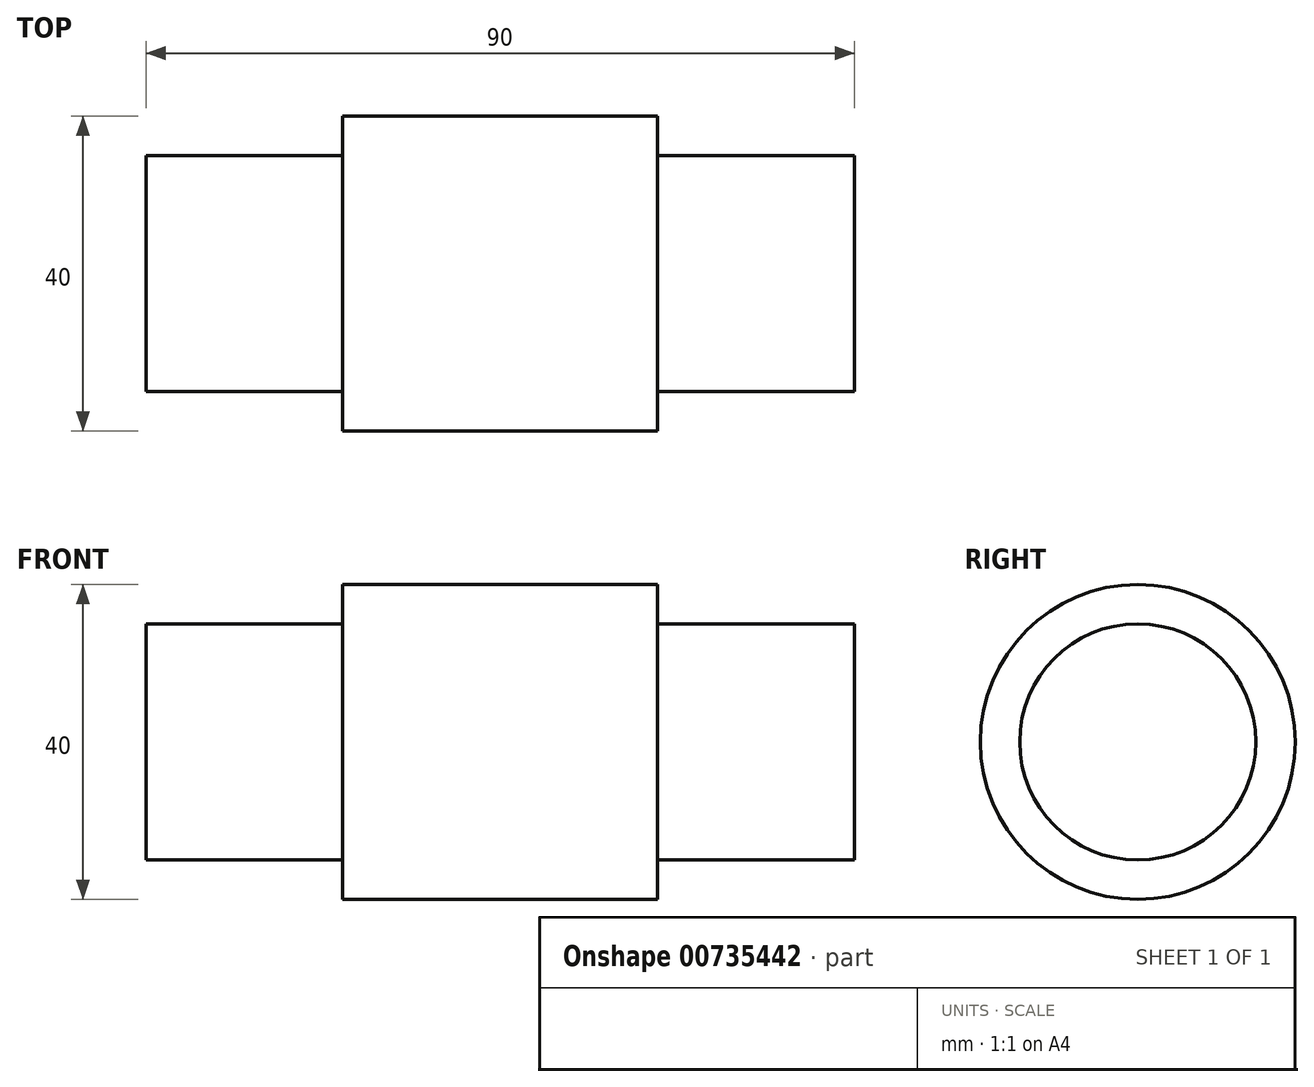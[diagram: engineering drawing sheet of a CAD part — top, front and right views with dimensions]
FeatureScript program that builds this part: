
annotation { "Feature Type Name" : "Feature", "Feature Type Description" : "" }
export const myFeature = defineFeature(function(context is Context, id is Id, definition is map)
    precondition{}
    {
        {
            var Q0;
            Q0=qCreatedBy(makeId("Top.planeOp"),FACE);
            var sketch = newSketch(context, id + "F0", { "sketchPlane" : qUnion([Q0])});
            skLineSegment(sketch, "E0", {"start": v(24.33, 1.06) * mm, "end": v(24.33, 16.06) * mm});
            skLineSegment(sketch, "E1", {"start": v(24.33, 16.06) * mm, "end": v(-25.67, 16.06) * mm});
            skLineSegment(sketch, "E2", {"start": v(24.33, 16.06) * mm, "end": v(19.33, 16.06) * mm});
            skLineSegment(sketch, "E3", {"start": v(-25.67, 16.06) * mm, "end": v(-20.67, 16.06) * mm});
            skLineSegment(sketch, "E4", {"start": v(-20.67, 16.06) * mm, "end": v(-15.67, 16.06) * mm});
            skLineSegment(sketch, "E5", {"start": v(19.33, 16.06) * mm, "end": v(14.33, 16.06) * mm});
            skPoint(sketch, "E6.1.internal.snap0", {"position": v(-0.67, 16.06) * mm});
            skLineSegment(sketch, "E7", {"start": v(19.33, 16.06) * mm, "end": v(19.33, 21.06) * mm});
            skLineSegment(sketch, "E8", {"start": v(24.33, 16.06) * mm, "end": v(19.33, 21.06) * mm});
            skLineSegment(sketch, "E9", {"start": v(19.33, 21.06) * mm, "end": v(-20.67, 21.06) * mm});
            skLineSegment(sketch, "E10", {"start": v(-20.67, 21.06) * mm, "end": v(-20.67, 16.06) * mm});
            skLineSegment(sketch, "E11", {"start": v(-20.67, 21.06) * mm, "end": v(-25.67, 16.06) * mm});
            skLineSegment(sketch, "E12", {"start": v(24.33, 1.06) * mm, "end": v(-25.67, 1.06) * mm});
            skLineSegment(sketch, "E13.MirrorCS", {"start": v(24.33, -13.94) * mm, "end": v(19.3, -13.94) * mm});
            skLineSegment(sketch, "E14.MirrorCS", {"start": v(24.3, -13.94) * mm, "end": v(19.3, -18.94) * mm});
            skLineSegment(sketch, "E15.MirrorCS", {"start": v(19.3, -13.94) * mm, "end": v(19.3, -18.94) * mm});
            skLineSegment(sketch, "E16.MirrorCS", {"start": v(-20.7, -18.94) * mm, "end": v(-25.7, -13.94) * mm});
            skLineSegment(sketch, "E17.MirrorCS", {"start": v(-20.7, -18.94) * mm, "end": v(-20.7, -13.94) * mm});
            skLineSegment(sketch, "E18.MirrorCS", {"start": v(-20.7, -13.94) * mm, "end": v(-15.7, -13.94) * mm});
            skLineSegment(sketch, "E19.MirrorCS", {"start": v(-25.7, -13.94) * mm, "end": v(-20.7, -13.94) * mm});
            skLineSegment(sketch, "E20.MirrorCS", {"start": v(19.3, -13.94) * mm, "end": v(14.3, -13.94) * mm});
            skLineSegment(sketch, "E21.MirrorCS", {"start": v(-25.67, 1.06) * mm, "end": v(-25.67, -13.94) * mm});
            skLineSegment(sketch, "E22.MirrorCS", {"start": v(24.3, -13.94) * mm, "end": v(-25.7, -13.94) * mm});
            skLineSegment(sketch, "E23.MirrorCS", {"start": v(19.3, -18.94) * mm, "end": v(-20.7, -18.94) * mm});
            skPoint(sketch, "E24.MirrorP", {"position": v(-0.67, -13.94) * mm});
            skLineSegment(sketch, "E25", {"start": v(24.33, 1.06) * mm, "end": v(24.33, -13.94) * mm});
            skLineSegment(sketch, "E26", {"start": v(-25.67, 16.06) * mm, "end": v(-25.67, 1.06) * mm});
            skLineSegment(sketch, "E27", {"start": v(-25.67, 16.06) * mm, "end": v(-45.67, 16.06) * mm});
            skLineSegment(sketch, "E28", {"start": v(-45.67, 16.06) * mm, "end": v(-45.67, -13.94) * mm});
            skLineSegment(sketch, "E29", {"start": v(-45.67, -13.94) * mm, "end": v(-25.7, -13.94) * mm});
            skLineSegment(sketch, "E30", {"start": v(-25.67, 1.06) * mm, "end": v(-45.67, 1.06) * mm});
            skLineSegment(sketch, "E31", {"start": v(24.33, 16.06) * mm, "end": v(44.33, 16.06) * mm});
            skLineSegment(sketch, "E32", {"start": v(24.33, -13.94) * mm, "end": v(44.33, -13.94) * mm});
            skLineSegment(sketch, "E33", {"start": v(44.33, -13.94) * mm, "end": v(44.33, 16.06) * mm});
            skLineSegment(sketch, "E34", {"start": v(24.33, 1.06) * mm, "end": v(44.33, 1.06) * mm});
            skSolve(sketch);
        }
        {
            var Q0;
            Q0=makeQuery(id+"F0.imprint","IMPRINT",FACE,{"disambiguationData":[TD([[makeQuery(id+"F0.imprint","IMPRINT",EDGE,{"derivedFrom":sQuery(id+"F0.wireOp",EDGE,"E3")}),1.0]])]});
            var Q1;
            Q1=makeQuery(id+"F0.imprint","IMPRINT",FACE,{"disambiguationData":[TD([[makeQuery(id+"F0.imprint","IMPRINT",EDGE,{"derivedFrom":sQuery(id+"F0.wireOp",EDGE,"E1")}),-1.0]])]});
            var Q2;
            Q2=makeQuery(id+"F0.imprint","IMPRINT",FACE,{"disambiguationData":[TD([[makeQuery(id+"F0.imprint","IMPRINT",EDGE,{"derivedFrom":sQuery(id+"F0.wireOp",EDGE,"E2")}),-1.0]])]});
            var Q3;
            Q3=makeQuery(id+"F0.imprint","IMPRINT",FACE,{"disambiguationData":[TD([[makeQuery(id+"F0.imprint","IMPRINT",EDGE,{"derivedFrom":sQuery(id+"F0.wireOp",EDGE,"E0")}),1.0]])]});
            var Q4;
            Q4=makeQuery(id+"F0.imprint","IMPRINT",FACE,{"disambiguationData":[TD([[makeQuery(id+"F0.imprint","IMPRINT",EDGE,{"derivedFrom":sQuery(id+"F0.wireOp",EDGE,"E26")}),-1.0]])]});
            var Q5;
            Q5=makeQuery(id+"F0.imprint","IMPRINT",FACE,{"disambiguationData":[TD([[makeQuery(id+"F0.imprint","IMPRINT",EDGE,{"derivedFrom":sQuery(id+"F0.wireOp",EDGE,"E0")}),-1.0]])]});
            var Q6;
            Q6=sQuery(id+"F0.wireOp",EDGE,"E12");
            revolve(context, id + "F1", {"surfaceOperationType" : NewSurfaceOperationType.NEW, "entities" : qUnion([Q0, Q1, Q2, Q3, Q4, Q5]), "axis" : qUnion([Q6]), "revolveType" : RevolveType.FULL});
        }
    });
